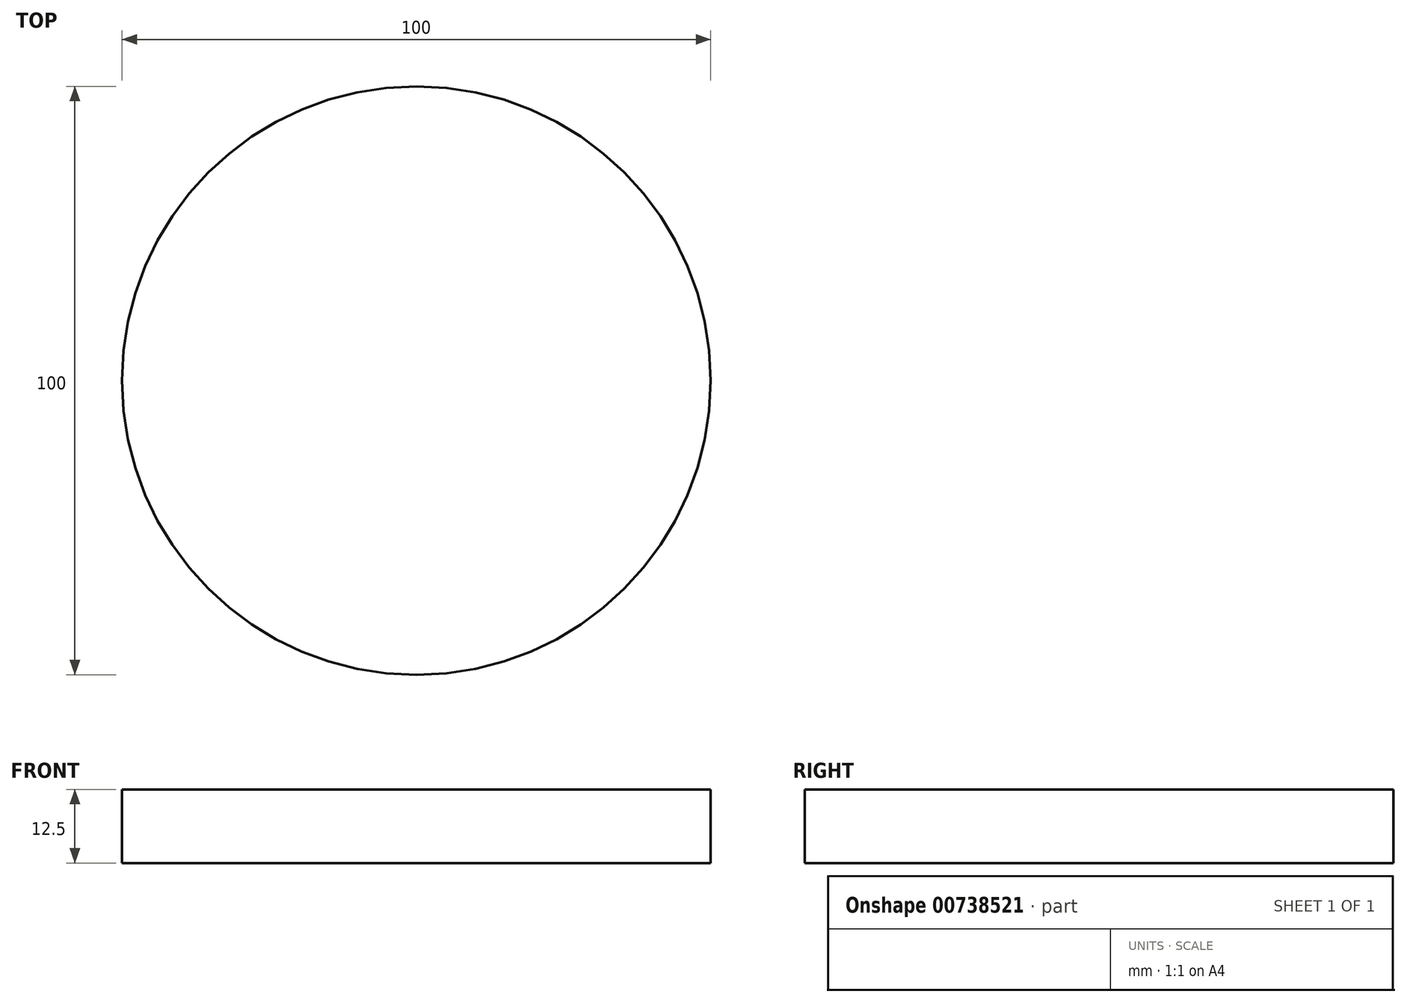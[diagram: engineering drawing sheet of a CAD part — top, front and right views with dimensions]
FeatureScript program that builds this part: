
annotation { "Feature Type Name" : "Feature", "Feature Type Description" : "" }
export const myFeature = defineFeature(function(context is Context, id is Id, definition is map)
    precondition{}
    {
        {
            var Q0;
            Q0=qCreatedBy(makeId("Top.planeOp"),FACE);
            var sketch = newSketch(context, id + "F0", { "sketchPlane" : qUnion([Q0])});
            skCircle(sketch, "E0", {"center": v(0, 0) * mm, "radius": 50 * mm});
            skSolve(sketch);
        }
        {
            var Q0;
            Q0=qSketchRegion(id+"F0",true);
            extrude(context, id + "F1", {"entities" : qUnion([Q0]), "depth" : 12.5 * mm, "offsetDistance" : 25 * mm});
        }
        {
            var Q0;
            Q0=makeQuery(id+"F1.opExtrude","SWEPT_BODY",BODY,{"disambiguationData":[OSD([sQuery(id+"F0.wireOp",EDGE,"E0")])]});
            transform(context, id + "F2", {"entities" : qUnion([Q0]), "transformType" : TransformType.TRANSLATION_3D, "dx" : 0 * mm, "dy" : 0 * mm, "dz" : 10 * mm, "makeCopy" : false});
        }
    });
